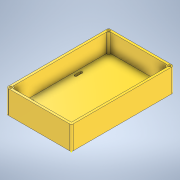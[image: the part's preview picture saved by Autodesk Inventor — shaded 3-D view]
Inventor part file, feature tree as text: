
AUTODESK INVENTOR PART (.ipt)
format: ipt  version: 2020 (Build 240168000, 168)  size: 267,264 bytes
history: native  units: mm
features: sketch x5, extrude x4, hole x1, fillet x1
ambient origin geometry x8: Origin, YZ Plane, XZ Plane, XY Plane, X Axis, Y Axis, Z Axis, Center Point
bodies: Solid1 (feature_tree)
feature tree (11):
  sketch  "Sketch1"  dims[d0=70.0mm d1=110.0mm]
  extrude  "Extrusion1"  Depth=110.0mm
  extrude  "Extrusion2"  Depth=105.0mm
  extrude  "Extrusion3"  Depth=52.5mm
  extrude  "Extrusion4"  Depth=16.21mm
  hole  "Hole1"  [1 undecoded]
  fillet  "Fillet2"  Radius=16.4mm
  sketch  "Sketch6"  dims[d8=3.0mm d9=2.5mm d10=16.4mm d11=3.55mm d12=3.0mm d13=2.5mm d14=19.89mm d15=16.4mm d16=3.9mm d17=16.21mm d18=16.4mm d19=3.55mm d20=3.0mm d21=2.5mm d22=3.0mm d23=2.5mm d24=25.0mm d25=0.0mm d26=5.0mm d27=0.0mm d28=3.0mm d29=4.0mm d30=3.0mm d31=4.0mm d32=3.0mm d33=4.0mm d34=3.0mm d35=90.0deg d36=4.0mm d37=1.0mm d38=0.0mm d40=5.0mm d41=24.0mm d42=0.0mm d43=3.0mm d44=6.0mm d45=3.5mm d46=2.0mm d47=90.0deg d48=40.0mm d49=20.594885mm d50=2.0mm]
  sketch  "Sketch2"  dims[d2=65.0mm d3=105.0mm]
  sketch  "Sketch3"  dims[d4=52.5mm d5=52.5mm]
  sketch  "Sketch5"  dims[d6=3.9mm d7=16.21mm]
note: 1 required parameter value undecoded (feature->parameter linkage not recoverable at this tier; creation-order binding heuristic only, values carry confidence <= 0.55)
